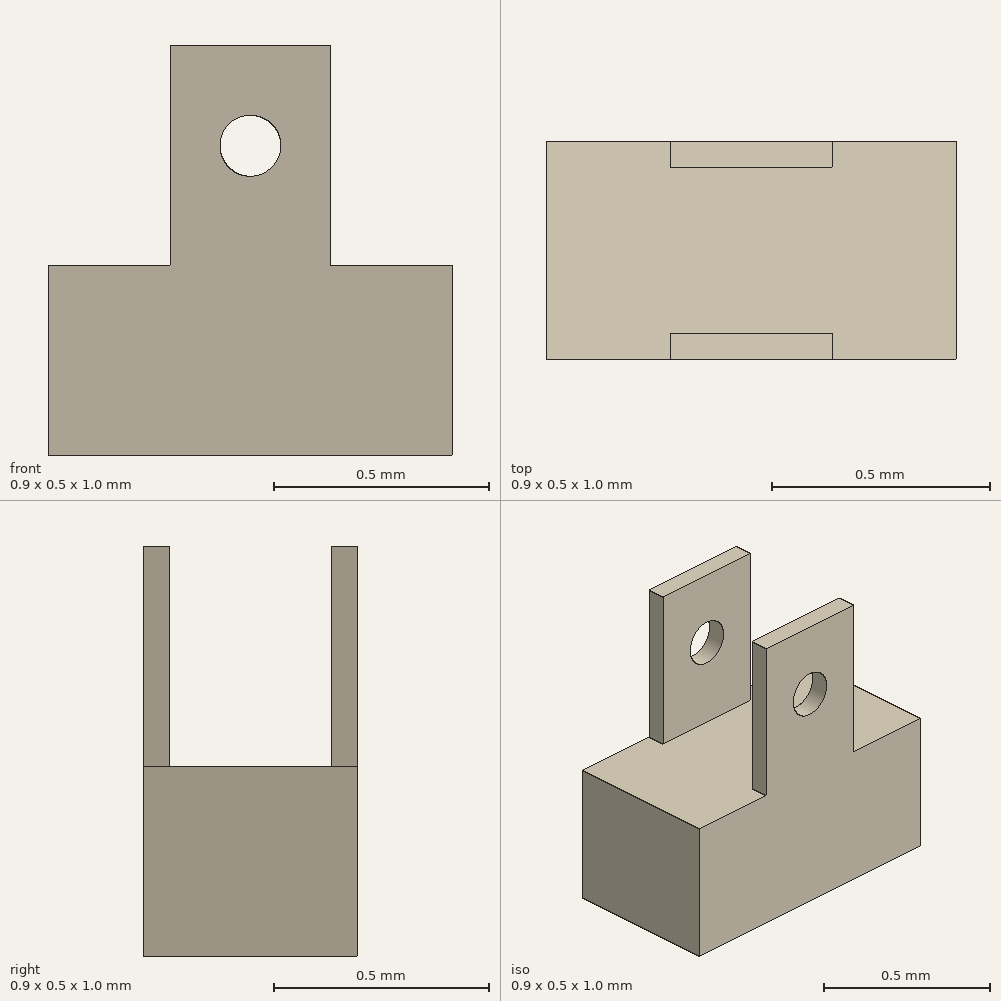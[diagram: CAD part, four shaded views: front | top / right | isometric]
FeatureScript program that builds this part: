
annotation { "Feature Type Name" : "Feature", "Feature Type Description" : "" }
export const myFeature = defineFeature(function(context is Context, id is Id, definition is map)
    precondition{}
    {
        {
            var Q0;
            Q0=qCreatedBy(makeId("Front.planeOp"),FACE);
            var sketch = newSketch(context, id + "F0", { "sketchPlane" : qUnion([Q0])});
            skLineSegment(sketch, "E0", {"start": v(0, 0) * mm, "end": v(0.94, 0) * mm});
            skLineSegment(sketch, "E1", {"start": v(0, 0) * mm, "end": v(0, 0.44) * mm});
            skLineSegment(sketch, "E2", {"start": v(0, 0.44) * mm, "end": v(0.94, 0.44) * mm});
            skLineSegment(sketch, "E3", {"start": v(0.94, 0.44) * mm, "end": v(0.94, 0) * mm});
            skLineSegment(sketch, "E4", {"start": v(0, 0.22) * mm, "end": v(0.94, 0.22) * mm});
            skLineSegment(sketch, "E5", {"start": v(0.47, 0.22) * mm, "end": v(0.47, 0.96) * mm});
            skLineSegment(sketch, "E6", {"start": v(0.47, 0.96) * mm, "end": v(0.66, 0.96) * mm});
            skLineSegment(sketch, "E7", {"start": v(0.47, 0.96) * mm, "end": v(0.28, 0.96) * mm});
            skLineSegment(sketch, "E8", {"start": v(0.66, 0.96) * mm, "end": v(0.66, 0.44) * mm});
            skLineSegment(sketch, "E9", {"start": v(0.28, 0.96) * mm, "end": v(0.28, 0.44) * mm});
            skCircle(sketch, "E10", {"center": v(0.47, 0.72) * mm, "radius": 0.07 * mm});
            skLineSegment(sketch, "E11", {"start": v(0.47, 0.72) * mm, "end": v(0.47, 0.22) * mm});
            skSolve(sketch);
        }
        {
            var Q0;
            Q0 = qSketchRegion(id + "F0", true);
            extrude(context, id + "F1", {"entities" : qUnion([Q0]), "depth" : .5 * mm});
        }
        {
            var Q0;
            Q0=makeQuery(id+"F1.opExtrude","SWEPT_FACE",FACE,{"disambiguationData":[OSD([sQuery(id+"F0.wireOp",EDGE,"E8")])]});
            var sketch = newSketch(context, id + "F2", { "sketchPlane" : qUnion([Q0])});
            skLineSegment(sketch, "E12", {"start": v(0, 0.96) * mm, "end": v(-0.06, 0.96) * mm});
            skLineSegment(sketch, "E13", {"start": v(-0.5, 0.96) * mm, "end": v(-0.44, 0.96) * mm});
            skLineSegment(sketch, "E14", {"start": v(-0.44, 0.96) * mm, "end": v(-0.44, 0.44) * mm});
            skLineSegment(sketch, "E15", {"start": v(-0.44, 0.44) * mm, "end": v(-0.06, 0.44) * mm});
            skLineSegment(sketch, "E16", {"start": v(-0.06, 0.96) * mm, "end": v(-0.06, 0.44) * mm});
            skLineSegment(sketch, "E17", {"start": v(-0.5, 0.96) * mm, "end": v(-0.61, 1.24) * mm});
            skLineSegment(sketch, "E18", {"start": v(-0.61, 1.24) * mm, "end": v(0.14, 1.14) * mm});
            skLineSegment(sketch, "E19", {"start": v(0.14, 1.14) * mm, "end": v(0, 0.96) * mm});
            skSolve(sketch);
        }
        {
            var Q0;
            {var subQ1=sQuery(id+"F2.wireOp",EDGE,"E12");Q0=makeQuery(id+"F2.imprint","IMPRINT",FACE,{"disambiguationData":[TD([[makeQuery(id+"F2.imprint","IMPRINT",EDGE,{"derivedFrom":subQ1}),1.0]])]});}
            var Q1;
            {var subQ0=sQuery(id+"F2.wireOp",EDGE,"E14");Q1=makeQuery(id+"F2.imprint","IMPRINT",FACE,{"disambiguationData":[TD([[makeQuery(id+"F2.imprint","IMPRINT",EDGE,{"derivedFrom":subQ0}),1.0]])]});}
            extrude(context, id + "F3", {"entities" : qUnion([Q0, Q1]), "operationType" : NewBodyOperationType.REMOVE, "oppositeDirection" : true, "depth" : 25 * mm});
        }
    });
